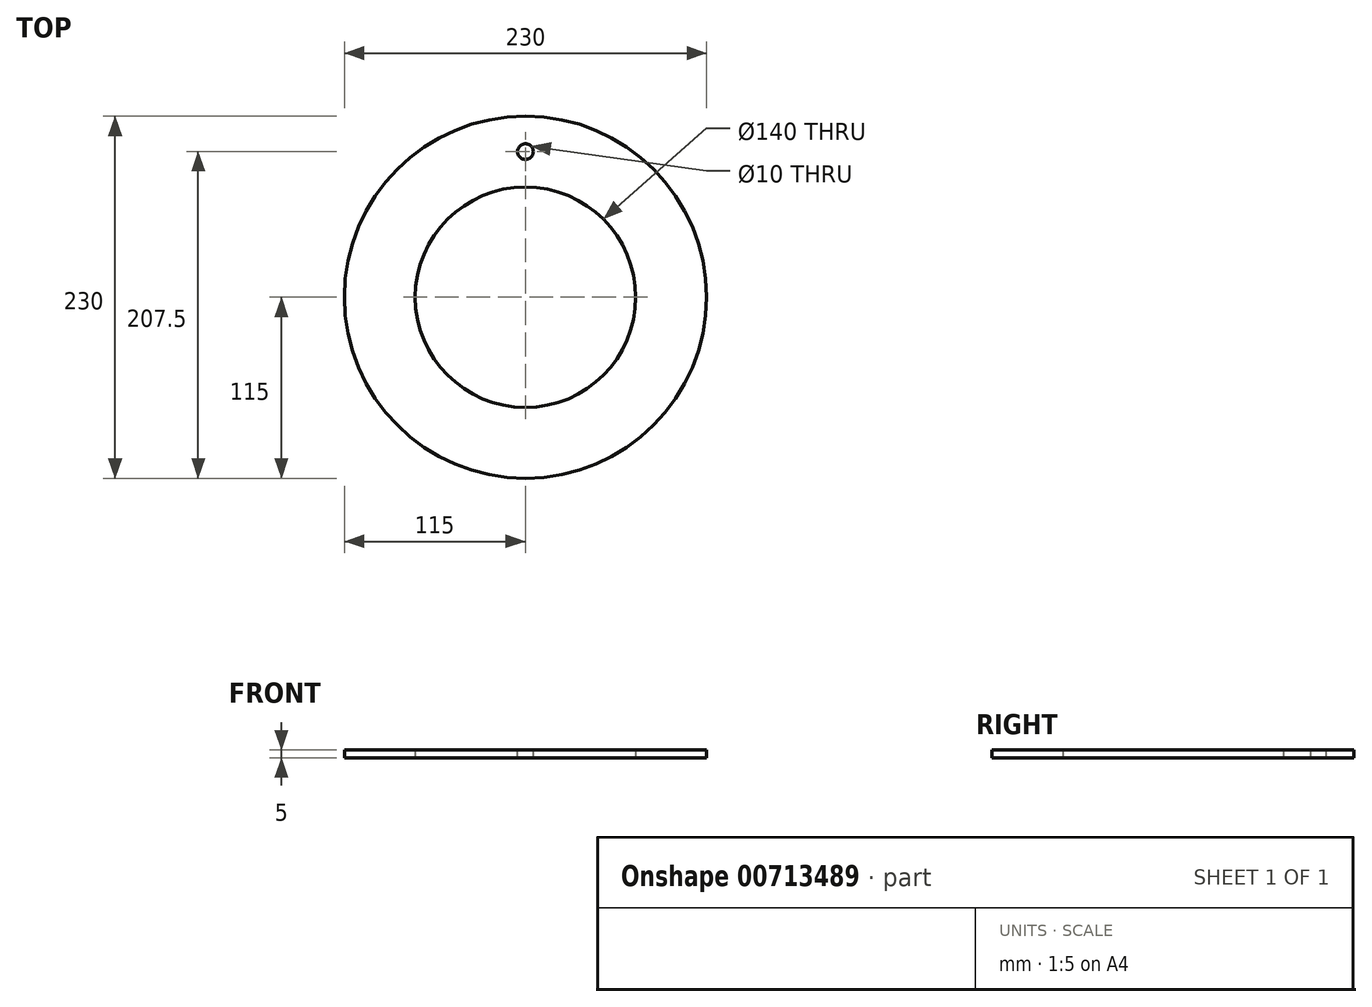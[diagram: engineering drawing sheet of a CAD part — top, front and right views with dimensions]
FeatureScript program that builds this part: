
annotation { "Feature Type Name" : "Feature", "Feature Type Description" : "" }
export const myFeature = defineFeature(function(context is Context, id is Id, definition is map)
    precondition{}
    {
        {
            var Q0;
            Q0=qCreatedBy(makeId("Top.planeOp"),FACE);
            var sketch = newSketch(context, id + "F0", { "sketchPlane" : qUnion([Q0])});
            skCircle(sketch, "E0", {"center": v(0, 0) * mm, "radius": 70 * mm});
            skCircle(sketch, "E1", {"center": v(0, 0) * mm, "radius": 115 * mm});
            skSolve(sketch);
        }
        {
            var Q0;
            Q0=makeQuery(id+"F0.imprint","IMPRINT",FACE,{"disambiguationData":[TD([[makeQuery(id+"F0.imprint","IMPRINT",EDGE,{"derivedFrom":sQuery(id+"F0.wireOp",EDGE,"E0")}),-1.0]])]});
            extrude(context, id + "F1", {"entities" : qUnion([Q0]), "depth" : 5 * mm, "offsetDistance" : 25 * mm});
        }
        {
            var Q0;
            Q0=makeQuery(id+"F1.opExtrude","CAP_FACE",FACE,{"disambiguationData":[OSD([sQuery(id+"F0.wireOp",EDGE,"E0"),sQuery(id+"F0.wireOp",EDGE,"E1")])],"isStart":false});
            var sketch = newSketch(context, id + "F2", { "sketchPlane" : qUnion([Q0])});
            skCircle(sketch, "E2", {"center": v(0, 92.5) * mm, "radius": 5 * mm});
            skLineSegment(sketch, "E3", {"start": v(0, 92.5) * mm, "end": v(0, 0) * mm, "construction": true});
            skSolve(sketch);
        }
        {
            var Q0;
            Q0 = qSketchRegion(id + "F2", true);
            extrude(context, id + "F3", {"entities" : qUnion([Q0]), "operationType" : NewBodyOperationType.REMOVE, "oppositeDirection" : true, "depth" : 25 * mm, "offsetDistance" : 25 * mm});
        }
    });
